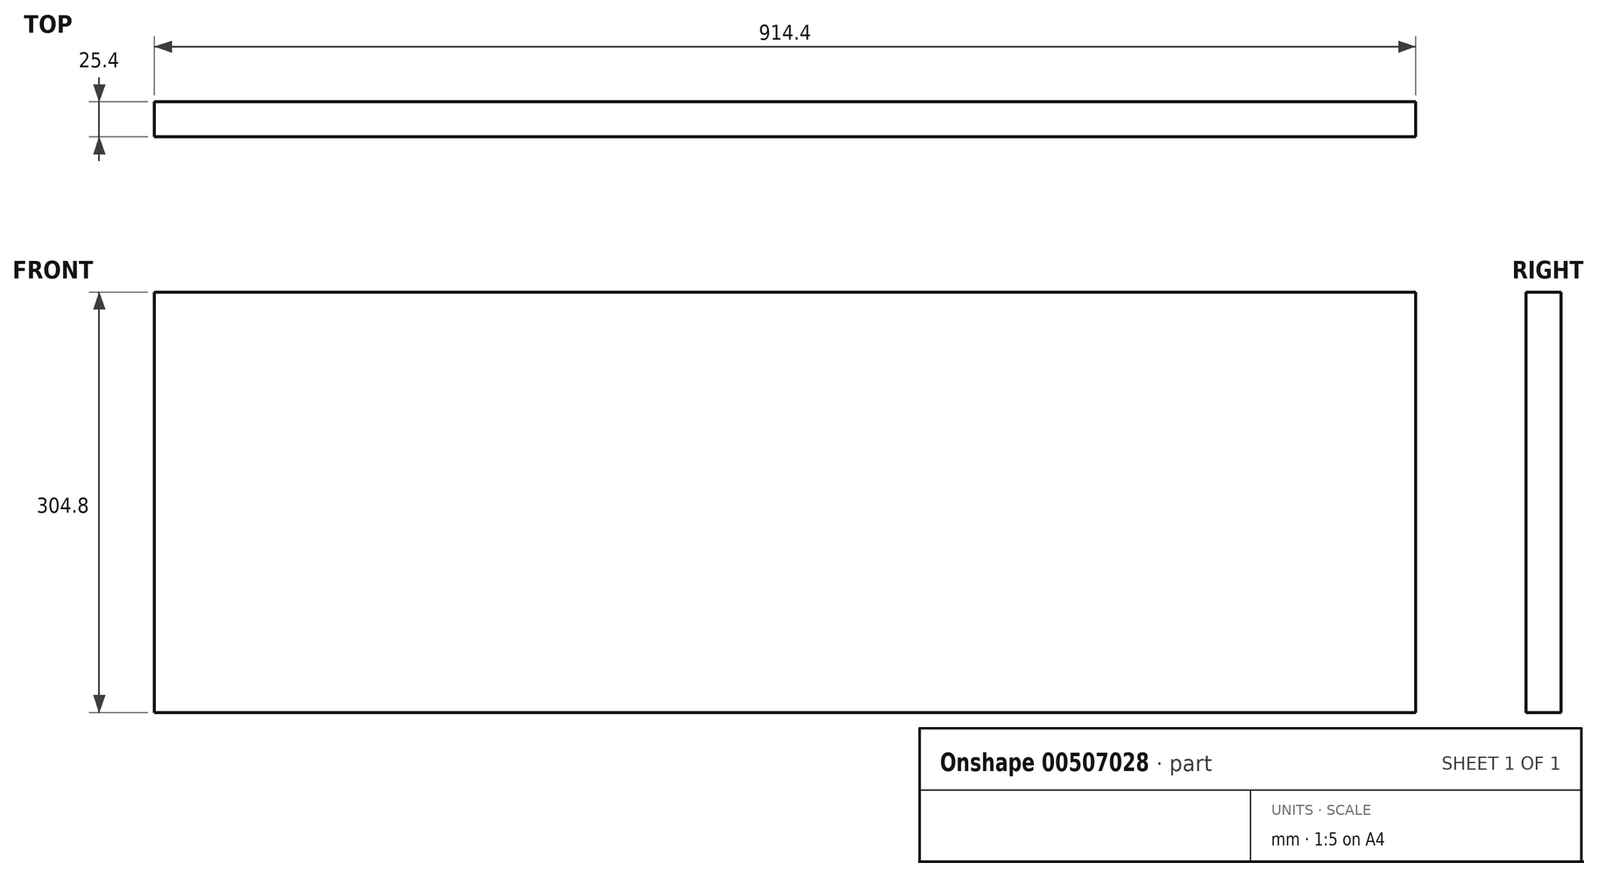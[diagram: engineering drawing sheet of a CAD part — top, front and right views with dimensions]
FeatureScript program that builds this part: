
annotation { "Feature Type Name" : "Feature", "Feature Type Description" : "" }
export const myFeature = defineFeature(function(context is Context, id is Id, definition is map)
    precondition{}
    {
        {
            var Q0;
            Q0=qCreatedBy(makeId("Front.planeOp"),FACE);
            var sketch = newSketch(context, id + "F0", { "sketchPlane" : qUnion([Q0])});
            skLineSegment(sketch, "E0.bottom", {"start": v(759.77, -128.73) * mm, "end": v(-154.63, -128.73) * mm});
            skLineSegment(sketch, "E0.top", {"start": v(759.77, 176.07) * mm, "end": v(-154.63, 176.07) * mm});
            skLineSegment(sketch, "E0.left", {"start": v(759.77, -128.73) * mm, "end": v(759.77, 176.07) * mm});
            skLineSegment(sketch, "E0.right", {"start": v(-154.63, -128.73) * mm, "end": v(-154.63, 176.07) * mm});
            skSolve(sketch);
        }
        {
            var Q0;
            Q0=makeQuery(id+"F0.imprint","IMPRINT",FACE,{"disambiguationData":[TD([[makeQuery(id+"F0.imprint","IMPRINT",EDGE,{"derivedFrom":sQuery(id+"F0.wireOp",EDGE,"E0.bottom")}),-1.0]])]});
            extrude(context, id + "F1", {"entities" : qUnion([Q0]), "depth" : 25.4 * mm});
        }
    });
